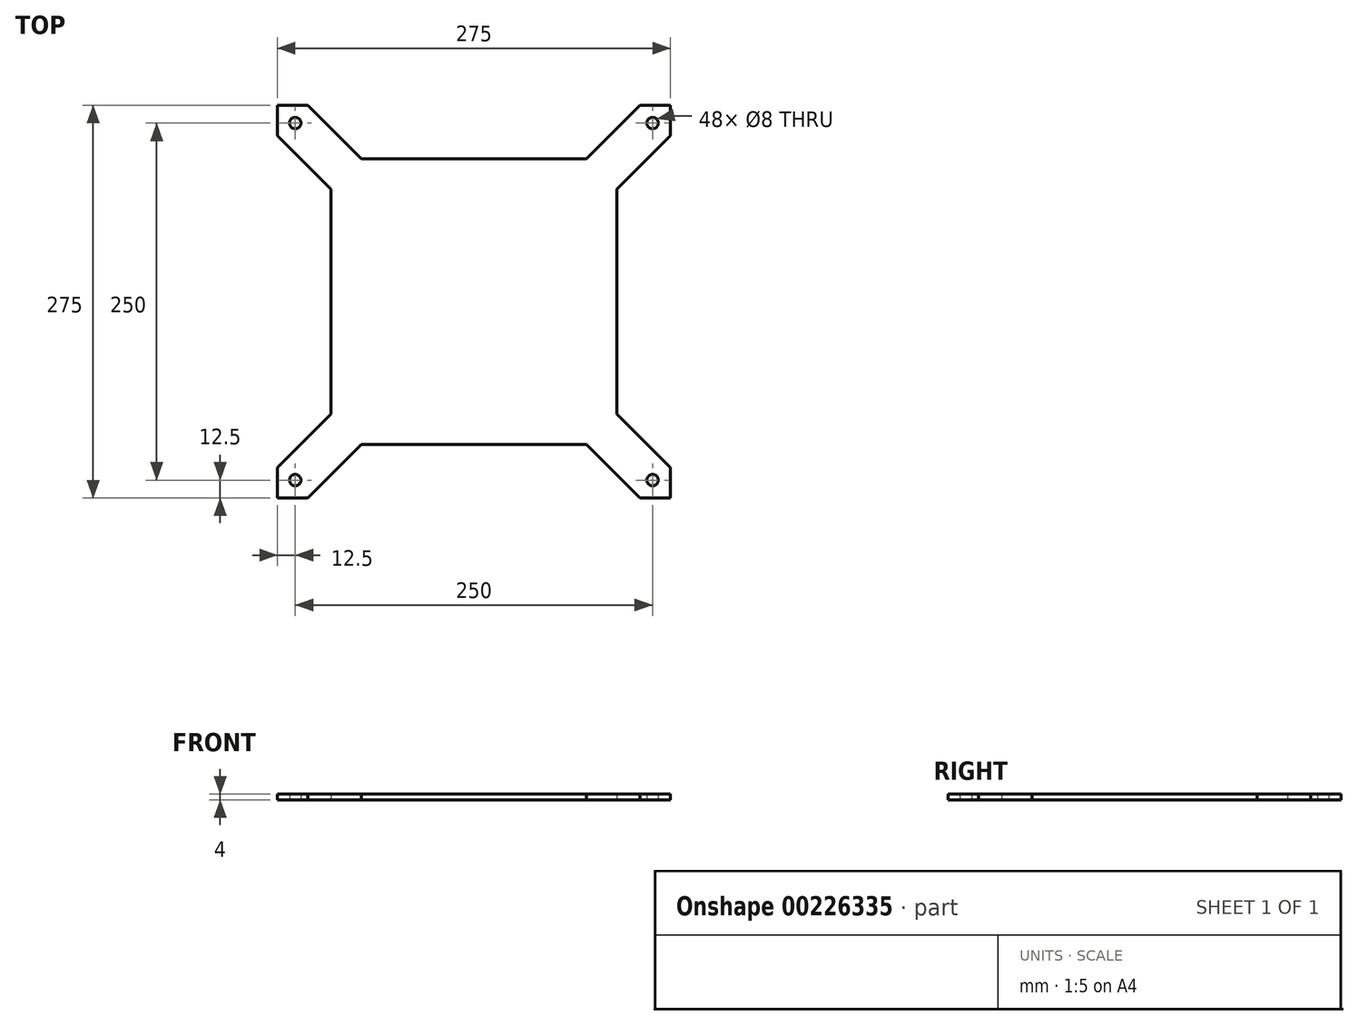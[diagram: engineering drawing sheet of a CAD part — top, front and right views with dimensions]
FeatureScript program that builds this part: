
annotation { "Feature Type Name" : "Feature", "Feature Type Description" : "" }
export const myFeature = defineFeature(function(context is Context, id is Id, definition is map)
    precondition{}
    {
        {
            var Q0;
            Q0=qCreatedBy(makeId("Top.planeOp"),FACE);
            var sketch = newSketch(context, id + "F0", { "sketchPlane" : qUnion([Q0])});
            skLineSegment(sketch, "E0.bottom", {"start": v(137.5, -137.5) * mm, "end": v(116.29, -137.5) * mm});
            skLineSegment(sketch, "E0.top", {"start": v(137.5, 137.5) * mm, "end": v(116.29, 137.5) * mm});
            skLineSegment(sketch, "E0.left", {"start": v(137.5, -137.5) * mm, "end": v(137.5, -116.29) * mm});
            skLineSegment(sketch, "E0.right", {"start": v(-137.5, -137.5) * mm, "end": v(-137.5, -116.29) * mm});
            skPoint(sketch, "E0.middle", {"position": v(0, 0) * mm});
            skLineSegment(sketch, "E1.bottom", {"start": v(100, -100) * mm, "end": v(-100, -100) * mm});
            skLineSegment(sketch, "E1.top", {"start": v(100, 100) * mm, "end": v(-100, 100) * mm});
            skLineSegment(sketch, "E1.left", {"start": v(100, -100) * mm, "end": v(100, 100) * mm});
            skLineSegment(sketch, "E1.right", {"start": v(-100, -100) * mm, "end": v(-100, 100) * mm});
            skLineSegment(sketch, "E2.trimOffspring", {"start": v(78.79, -100) * mm, "end": v(116.29, -137.5) * mm});
            skLineSegment(sketch, "E3.trimOffspring", {"start": v(100, -78.79) * mm, "end": v(137.5, -116.29) * mm});
            skLineSegment(sketch, "E4.trimOffspring", {"start": v(100, 78.79) * mm, "end": v(137.5, 116.29) * mm});
            skLineSegment(sketch, "E5.trimOffspring", {"start": v(78.79, 100) * mm, "end": v(116.29, 137.5) * mm});
            skLineSegment(sketch, "E6.trimOffspring", {"start": v(-78.79, 100) * mm, "end": v(-116.29, 137.5) * mm});
            skLineSegment(sketch, "E7.trimOffspring", {"start": v(-100, 78.79) * mm, "end": v(-137.5, 116.29) * mm});
            skLineSegment(sketch, "E8.trimOffspring", {"start": v(-100, -78.79) * mm, "end": v(-137.5, -116.29) * mm});
            skLineSegment(sketch, "E9.trimOffspring", {"start": v(-78.79, -100) * mm, "end": v(-116.29, -137.5) * mm});
            skLineSegment(sketch, "E10.trimOffspring", {"start": v(137.5, 116.29) * mm, "end": v(137.5, 137.5) * mm});
            skLineSegment(sketch, "E11.trimOffspring", {"start": v(-116.29, -137.5) * mm, "end": v(-137.5, -137.5) * mm});
            skLineSegment(sketch, "E12.trimOffspring", {"start": v(-137.5, 116.29) * mm, "end": v(-137.5, 137.5) * mm});
            skLineSegment(sketch, "E13.trimOffspring", {"start": v(-116.29, 137.5) * mm, "end": v(-137.5, 137.5) * mm});
            skLineSegment(sketch, "E14.bottom", {"start": v(-137.5, 137.5) * mm, "end": v(-116.29, 137.5) * mm});
            skLineSegment(sketch, "E14.top", {"start": v(-133.71, 112.5) * mm, "end": v(-112.5, 112.5) * mm});
            skLineSegment(sketch, "E14.left", {"start": v(-137.5, 137.5) * mm, "end": v(-137.5, 116.29) * mm});
            skLineSegment(sketch, "E14.right", {"start": v(-112.5, 133.71) * mm, "end": v(-112.5, 112.5) * mm});
            skLineSegment(sketch, "E15", {"start": v(-137.5, 137.5) * mm, "end": v(-127.83, 127.83) * mm});
            skCircle(sketch, "E16", {"center": v(-125, 125) * mm, "radius": 4 * mm});
            skLineSegment(sketch, "E17.top", {"start": v(133.71, 112.5) * mm, "end": v(112.5, 112.5) * mm});
            skLineSegment(sketch, "E17.left", {"start": v(137.5, 137.5) * mm, "end": v(137.5, 116.29) * mm});
            skLineSegment(sketch, "E17.right", {"start": v(112.5, 133.71) * mm, "end": v(112.5, 112.5) * mm});
            skLineSegment(sketch, "E18", {"start": v(137.5, 137.5) * mm, "end": v(127.83, 127.83) * mm});
            skCircle(sketch, "E19", {"center": v(125, 125) * mm, "radius": 4 * mm});
            skLineSegment(sketch, "E20.top", {"start": v(133.71, -112.5) * mm, "end": v(112.5, -112.5) * mm});
            skLineSegment(sketch, "E20.right", {"start": v(112.5, -133.71) * mm, "end": v(112.5, -112.5) * mm});
            skLineSegment(sketch, "E21", {"start": v(137.5, -137.5) * mm, "end": v(127.83, -127.83) * mm});
            skCircle(sketch, "E22", {"center": v(125, -125) * mm, "radius": 4 * mm});
            skLineSegment(sketch, "E23.bottom", {"start": v(-137.5, -137.5) * mm, "end": v(-116.29, -137.5) * mm});
            skLineSegment(sketch, "E23.top", {"start": v(-133.71, -112.5) * mm, "end": v(-112.5, -112.5) * mm});
            skLineSegment(sketch, "E23.right", {"start": v(-112.5, -133.71) * mm, "end": v(-112.5, -112.5) * mm});
            skLineSegment(sketch, "E24", {"start": v(-137.5, -137.5) * mm, "end": v(-127.83, -127.83) * mm});
            skCircle(sketch, "E25", {"center": v(-125, -125) * mm, "radius": 4 * mm});
            skSolve(sketch);
        }
        {
            var Q0;
            Q0 = qSketchRegion(id + "F0", true);
            extrude(context, id + "F1", {"entities" : qUnion([Q0]), "depth" : 4 * mm});
        }
    });
